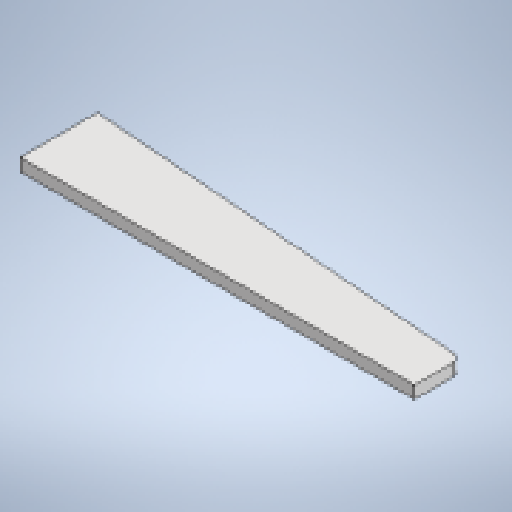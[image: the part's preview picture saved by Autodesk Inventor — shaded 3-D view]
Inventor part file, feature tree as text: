
AUTODESK INVENTOR PART (.ipt)
format: ipt  version: 2025.1 (Build 291241020, 241B)  size: 165,376 bytes
history: native  units: mm
features: other x2, sheet_metal_op x1, chamfer x1, sketch x1
ambient origin geometry x8: Origin, YZ Plane, XZ Plane, XY Plane, X Axis, Y Axis, Z Axis, Center Point
bodies: Body1 (feature_tree)
feature tree (5):
  sheet_metal_op  "Face1"
  chamfer  "Corner Round1"
  sketch  "Sketch3"  dims[d11=300.0mm d12=30.0mm d13=45.0mm d14=50.0mm d15=8.0mm d16=6.0mm]
  other  "Plate1"
  other  "Definition1"
